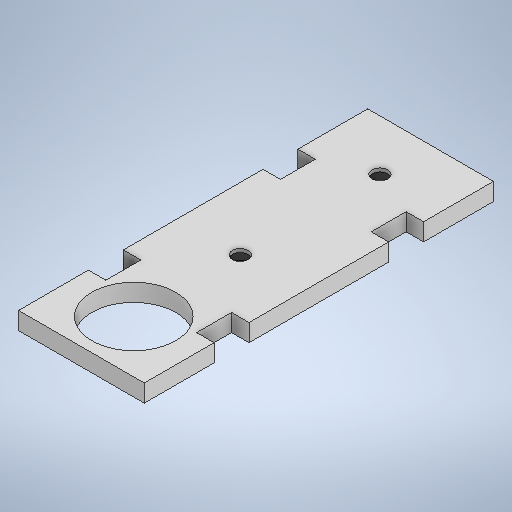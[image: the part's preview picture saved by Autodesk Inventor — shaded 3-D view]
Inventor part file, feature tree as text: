
AUTODESK INVENTOR PART (.ipt)
format: ipt  version: 2025.2 (Build 292293000, 293)  size: 275,456 bytes
history: native  units: mm
features: extrude x2, sketch x2
ambient origin geometry x8: Origin, YZ Plane, XZ Plane, XY Plane, X Axis, Y Axis, Z Axis, Center Point
bodies: Solid1 (feature_tree)
feature tree (4):
  extrude  "Extrusion1"  Depth=100.0mm
  extrude  "Extrusion2"  Depth=20.0mm
  sketch  "Sketch2"  dims[d0=36.0mm d1=100.0mm]
  sketch  "Sketch3"  dims[d2=20.0mm d3=20.0mm d4=10.0mm d5=5.0mm d6=10.0mm d7=5.0mm d8=5.0mm d9=15.0mm d10=24.0mm d15=5.0mm d16=0.0mm d17=30.5mm d18=10.1mm d19=40.0mm d20=10.1mm d21=4.5mm d22=4.5mm d23=1.0mm d24=0.0mm]
